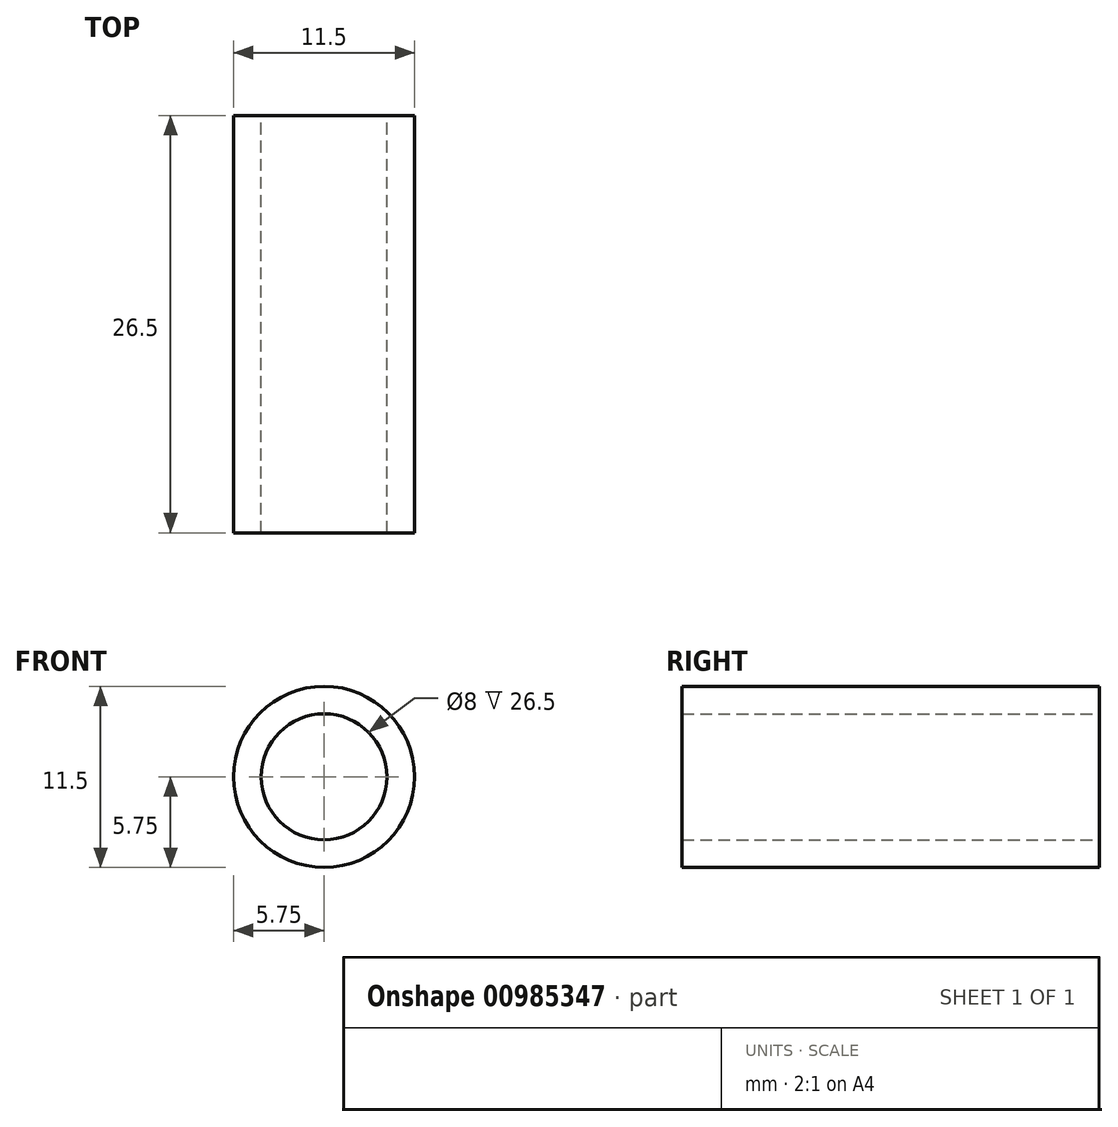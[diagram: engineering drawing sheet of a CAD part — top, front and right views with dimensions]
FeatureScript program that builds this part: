
annotation { "Feature Type Name" : "Feature", "Feature Type Description" : "" }
export const myFeature = defineFeature(function(context is Context, id is Id, definition is map)
    precondition{}
    {
        {
            var Q0;
            Q0=qCreatedBy(makeId("Front.planeOp"),FACE);
            var sketch = newSketch(context, id + "F0", { "sketchPlane" : qUnion([Q0])});
            skCircle(sketch, "E0", {"center": v(0, 0) * mm, "radius": 5.75 * mm});
            skCircle(sketch, "E1", {"center": v(0, 0) * mm, "radius": 4 * mm});
            skSolve(sketch);
        }
        {
            var Q0;
            Q0=qSketchRegion(id+"F0",true);
            extrude(context, id + "F1", {"entities" : qUnion([Q0]), "depth" : 26.5 * mm});
        }
    });
